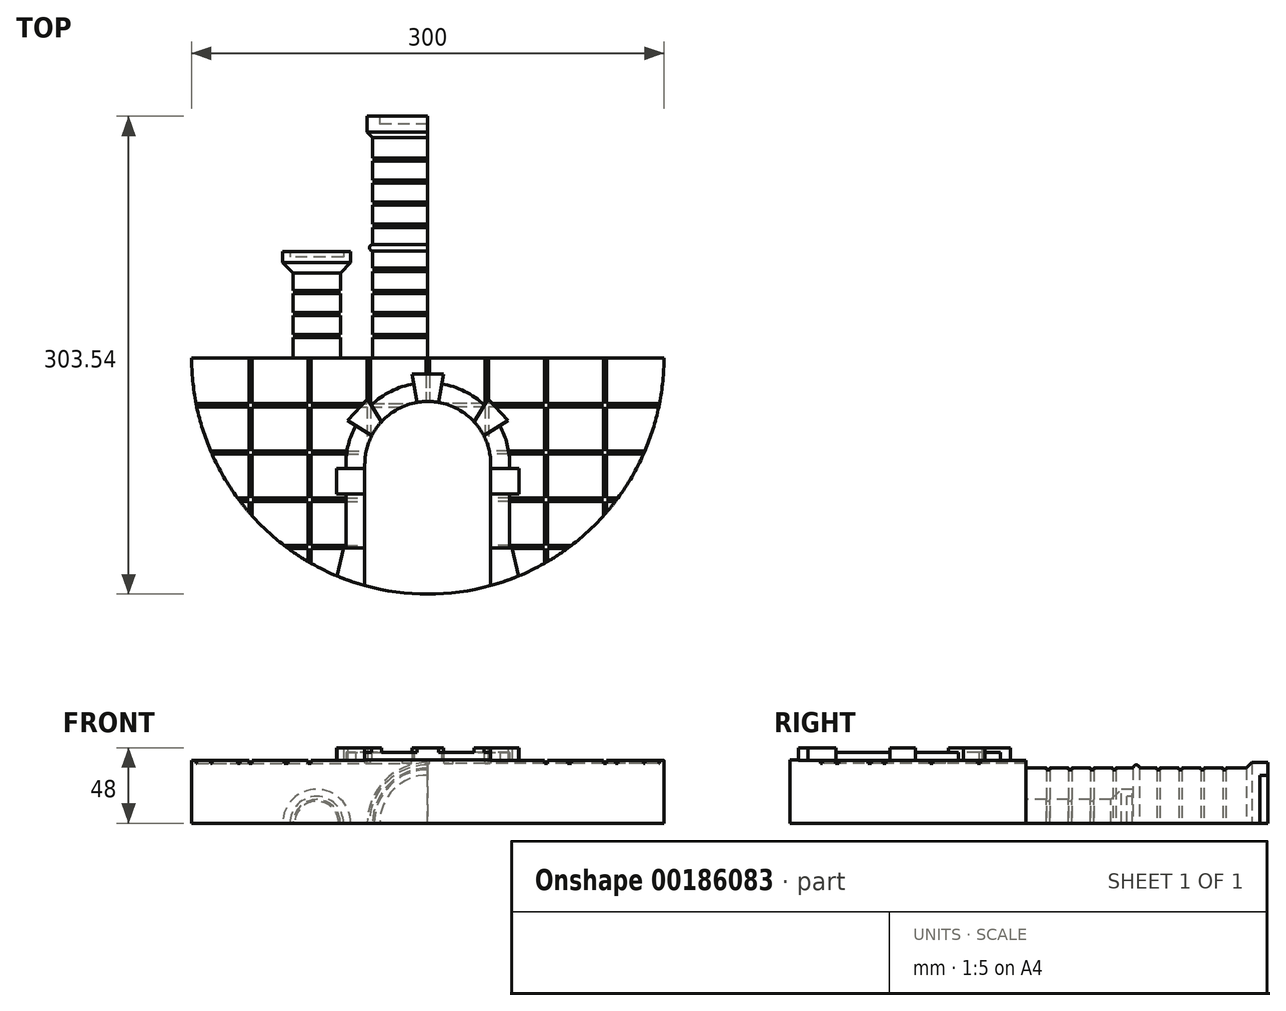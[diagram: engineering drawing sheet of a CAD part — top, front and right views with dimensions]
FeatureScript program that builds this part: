
annotation { "Feature Type Name" : "Feature", "Feature Type Description" : "" }
export const myFeature = defineFeature(function(context is Context, id is Id, definition is map)
    precondition{}
    {
        {
            var Q0;
            Q0=qCreatedBy(makeId("Top.planeOp"),FACE);
            var sketch = newSketch(context, id + "F0", { "sketchPlane" : qUnion([Q0])});
            skLineSegment(sketch, "E0", {"start": v(0, 136.15) * mm, "end": v(0, -317.95) * mm, "construction": true});
            skLineSegment(sketch, "E1.0", {"start": v(-150, 44.84) * mm, "end": v(-150, -145.55) * mm});
            skLineSegment(sketch, "E2", {"start": v(-150, 44.84) * mm, "end": v(0, 44.84) * mm});
            skArc(sketch, "E3", {"start": v(-150, -145.55) * mm, "mid": v(-106.07, -251.62) * mm, "end": v(0, -295.55) * mm});
            skLineSegment(sketch, "E4", {"start": v(-157.24, -145.55) * mm, "end": v(0, -145.55) * mm});
            skLineSegment(sketch, "E5", {"start": v(0, -145.55) * mm, "end": v(0, -295.55) * mm});
            skSolve(sketch);
        }
        {
            var Q0;
            Q0 = qSketchRegion(id + "F0", true);
            extrude(context, id + "F1", {"entities" : qUnion([Q0]), "depth" : 40 * mm});
        }
        {
            var Q0;
            Q0=makeQuery(id+"F1.opExtrude","CAP_FACE",FACE,{"disambiguationData":[OSD([sQuery(id+"F0.wireOp",EDGE,"E3"),sQuery(id+"F0.wireOp",EDGE,"E4"),sQuery(id+"F0.wireOp",EDGE,"E5")])],"isStart":false});
            var sketch = newSketch(context, id + "F2", { "sketchPlane" : qUnion([Q0])});
            skLineSegment(sketch, "E6.0", {"start": v(-150, -174.55) * mm, "end": v(0, -174.55) * mm});
            skLineSegment(sketch, "E7.0", {"start": v(-150, -176.55) * mm, "end": v(0, -176.55) * mm});
            skLineSegment(sketch, "E8.0", {"start": v(-150, -204.55) * mm, "end": v(0, -204.55) * mm});
            skLineSegment(sketch, "E9.0", {"start": v(-150, -206.55) * mm, "end": v(0, -206.55) * mm});
            skLineSegment(sketch, "E10.0", {"start": v(-150, -234.55) * mm, "end": v(0, -234.55) * mm});
            skLineSegment(sketch, "E11.0", {"start": v(-150, -236.55) * mm, "end": v(0, -236.55) * mm});
            skLineSegment(sketch, "E12.0", {"start": v(-150, -264.55) * mm, "end": v(0, -264.55) * mm});
            skLineSegment(sketch, "E13.0", {"start": v(-150, -266.55) * mm, "end": v(0, -266.55) * mm});
            skLineSegment(sketch, "E14.0", {"start": v(-1, -140.7) * mm, "end": v(-1, -302.51) * mm});
            skLineSegment(sketch, "E15.0", {"start": v(-38.5, -140.42) * mm, "end": v(-38.5, -295.55) * mm});
            skLineSegment(sketch, "E16.0", {"start": v(-36.5, -139.03) * mm, "end": v(-36.5, -295.55) * mm});
            skLineSegment(sketch, "E17.0", {"start": v(-76, -139.3) * mm, "end": v(-76, -295.55) * mm});
            skLineSegment(sketch, "E18.0", {"start": v(-74, -139.03) * mm, "end": v(-74, -295.55) * mm});
            skLineSegment(sketch, "E19.0", {"start": v(-111.5, -140.42) * mm, "end": v(-111.5, -295.55) * mm});
            skLineSegment(sketch, "E20.0", {"start": v(-113.5, -139.3) * mm, "end": v(-113.5, -295.55) * mm});
            skLineSegment(sketch, "E21", {"start": v(-1, -140.7) * mm, "end": v(2.08, -140.7) * mm});
            skLineSegment(sketch, "E22", {"start": v(2.08, -140.7) * mm, "end": v(2.08, -302.51) * mm});
            skLineSegment(sketch, "E23", {"start": v(2.08, -302.51) * mm, "end": v(-1, -302.51) * mm});
            skLineSegment(sketch, "E24", {"start": v(-113.5, -139.3) * mm, "end": v(-111.5, -140.42) * mm});
            skLineSegment(sketch, "E25", {"start": v(-76, -139.3) * mm, "end": v(-74, -139.03) * mm});
            skLineSegment(sketch, "E26", {"start": v(-38.5, -140.42) * mm, "end": v(-36.5, -139.03) * mm});
            skLineSegment(sketch, "E27", {"start": v(-38.5, -295.55) * mm, "end": v(-36.5, -295.55) * mm});
            skLineSegment(sketch, "E28", {"start": v(-74, -295.55) * mm, "end": v(-76, -295.55) * mm});
            skLineSegment(sketch, "E29", {"start": v(-111.5, -295.55) * mm, "end": v(-113.5, -295.55) * mm});
            skLineSegment(sketch, "E30", {"start": v(-150, -264.55) * mm, "end": v(-150, -266.55) * mm});
            skLineSegment(sketch, "E31", {"start": v(-150, -234.55) * mm, "end": v(-150, -236.55) * mm});
            skLineSegment(sketch, "E32", {"start": v(-150, -204.55) * mm, "end": v(-150, -206.55) * mm});
            skLineSegment(sketch, "E33", {"start": v(-150, -174.55) * mm, "end": v(-150, -176.55) * mm});
            skSolve(sketch);
        }
        {
            var Q0;
            {var subQ0=sQuery(id+"F2.wireOp",EDGE,"E30");Q0=makeQuery(id+"F2.imprint","IMPRINT",FACE,{"disambiguationData":[TD([[makeQuery(id+"F2.imprint","IMPRINT",EDGE,{"derivedFrom":subQ0}),1.0]])]});}
            var Q1;
            {var subQ5=sQuery(id+"F2.wireOp",EDGE,"E29");Q1=makeQuery(id+"F2.imprint","IMPRINT",FACE,{"disambiguationData":[TD([[makeQuery(id+"F2.imprint","IMPRINT",EDGE,{"derivedFrom":subQ5}),-1.0]])]});}
            var Q2;
            {var subQ0=sQuery(id+"F2.wireOp",EDGE,"E20.0");var subQ1=sQuery(id+"F2.wireOp",EDGE,"E6.0");var subQ2=makeQuery(id+"F2.imprint","INTERSECT",VERTEX,{"derivedFrom":[subQ1,subQ0]});Q2=makeQuery(id+"F2.imprint","IMPRINT",FACE,{"disambiguationData":[TD([[makeQuery(id+"F2.imprint","IMPRINT",EDGE,{"disambiguationData":[TD([[subQ2,-1.0]])],"derivedFrom":subQ1}),-1.0]])]});}
            var Q3;
            {var subQ0=sQuery(id+"F2.wireOp",EDGE,"E19.0");var subQ1=sQuery(id+"F2.wireOp",EDGE,"E6.0");var subQ2=makeQuery(id+"F2.imprint","INTERSECT",VERTEX,{"derivedFrom":[subQ1,subQ0]});Q3=makeQuery(id+"F2.imprint","IMPRINT",FACE,{"disambiguationData":[TD([[makeQuery(id+"F2.imprint","IMPRINT",EDGE,{"disambiguationData":[TD([[subQ2,-1.0]])],"derivedFrom":subQ1}),-1.0]])]});}
            var Q4;
            {var subQ0=sQuery(id+"F2.wireOp",EDGE,"E17.0");var subQ1=sQuery(id+"F2.wireOp",EDGE,"E6.0");var subQ2=makeQuery(id+"F2.imprint","INTERSECT",VERTEX,{"derivedFrom":[subQ1,subQ0]});Q4=makeQuery(id+"F2.imprint","IMPRINT",FACE,{"disambiguationData":[TD([[makeQuery(id+"F2.imprint","IMPRINT",EDGE,{"disambiguationData":[TD([[subQ2,-1.0]])],"derivedFrom":subQ1}),-1.0]])]});}
            var Q5;
            {var subQ0=sQuery(id+"F2.wireOp",EDGE,"E18.0");var subQ1=sQuery(id+"F2.wireOp",EDGE,"E6.0");var subQ2=makeQuery(id+"F2.imprint","INTERSECT",VERTEX,{"derivedFrom":[subQ1,subQ0]});Q5=makeQuery(id+"F2.imprint","IMPRINT",FACE,{"disambiguationData":[TD([[makeQuery(id+"F2.imprint","IMPRINT",EDGE,{"disambiguationData":[TD([[subQ2,-1.0]])],"derivedFrom":subQ1}),-1.0]])]});}
            var Q6;
            {var subQ0=sQuery(id+"F2.wireOp",EDGE,"E15.0");var subQ1=sQuery(id+"F2.wireOp",EDGE,"E6.0");var subQ2=makeQuery(id+"F2.imprint","INTERSECT",VERTEX,{"derivedFrom":[subQ1,subQ0]});Q6=makeQuery(id+"F2.imprint","IMPRINT",FACE,{"disambiguationData":[TD([[makeQuery(id+"F2.imprint","IMPRINT",EDGE,{"disambiguationData":[TD([[subQ2,-1.0]])],"derivedFrom":subQ1}),-1.0]])]});}
            var Q7;
            {var subQ0=sQuery(id+"F2.wireOp",EDGE,"E16.0");var subQ1=sQuery(id+"F2.wireOp",EDGE,"E6.0");var subQ2=makeQuery(id+"F2.imprint","INTERSECT",VERTEX,{"derivedFrom":[subQ1,subQ0]});Q7=makeQuery(id+"F2.imprint","IMPRINT",FACE,{"disambiguationData":[TD([[makeQuery(id+"F2.imprint","IMPRINT",EDGE,{"disambiguationData":[TD([[subQ2,-1.0]])],"derivedFrom":subQ1}),-1.0]])]});}
            var Q8;
            {var subQ0=sQuery(id+"F2.wireOp",EDGE,"E20.0");var subQ1=sQuery(id+"F2.wireOp",EDGE,"E7.0");var subQ2=makeQuery(id+"F2.imprint","INTERSECT",VERTEX,{"derivedFrom":[subQ1,subQ0]});Q8=makeQuery(id+"F2.imprint","IMPRINT",FACE,{"disambiguationData":[TD([[makeQuery(id+"F2.imprint","IMPRINT",EDGE,{"disambiguationData":[TD([[subQ2,-1.0]])],"derivedFrom":subQ1}),-1.0]])]});}
            var Q9;
            {var subQ0=sQuery(id+"F2.wireOp",EDGE,"E20.0");var subQ1=sQuery(id+"F2.wireOp",EDGE,"E8.0");var subQ2=makeQuery(id+"F2.imprint","INTERSECT",VERTEX,{"derivedFrom":[subQ1,subQ0]});Q9=makeQuery(id+"F2.imprint","IMPRINT",FACE,{"disambiguationData":[TD([[makeQuery(id+"F2.imprint","IMPRINT",EDGE,{"disambiguationData":[TD([[subQ2,-1.0]])],"derivedFrom":subQ1}),-1.0]])]});}
            var Q10;
            {var subQ0=sQuery(id+"F2.wireOp",EDGE,"E20.0");var subQ1=sQuery(id+"F2.wireOp",EDGE,"E9.0");var subQ2=makeQuery(id+"F2.imprint","INTERSECT",VERTEX,{"derivedFrom":[subQ1,subQ0]});Q10=makeQuery(id+"F2.imprint","IMPRINT",FACE,{"disambiguationData":[TD([[makeQuery(id+"F2.imprint","IMPRINT",EDGE,{"disambiguationData":[TD([[subQ2,-1.0]])],"derivedFrom":subQ1}),-1.0]])]});}
            var Q11;
            {var subQ0=sQuery(id+"F2.wireOp",EDGE,"E20.0");var subQ1=sQuery(id+"F2.wireOp",EDGE,"E12.0");var subQ2=makeQuery(id+"F2.imprint","INTERSECT",VERTEX,{"derivedFrom":[subQ1,subQ0]});Q11=makeQuery(id+"F2.imprint","IMPRINT",FACE,{"disambiguationData":[TD([[makeQuery(id+"F2.imprint","IMPRINT",EDGE,{"disambiguationData":[TD([[subQ2,-1.0]])],"derivedFrom":subQ1}),-1.0]])]});}
            var Q12;
            {var subQ0=sQuery(id+"F2.wireOp",EDGE,"E17.0");var subQ1=sQuery(id+"F2.wireOp",EDGE,"E12.0");var subQ2=makeQuery(id+"F2.imprint","INTERSECT",VERTEX,{"derivedFrom":[subQ1,subQ0]});Q12=makeQuery(id+"F2.imprint","IMPRINT",FACE,{"disambiguationData":[TD([[makeQuery(id+"F2.imprint","IMPRINT",EDGE,{"disambiguationData":[TD([[subQ2,-1.0]])],"derivedFrom":subQ1}),-1.0]])]});}
            var Q13;
            {var subQ0=sQuery(id+"F2.wireOp",EDGE,"E18.0");var subQ1=sQuery(id+"F2.wireOp",EDGE,"E12.0");var subQ2=makeQuery(id+"F2.imprint","INTERSECT",VERTEX,{"derivedFrom":[subQ1,subQ0]});Q13=makeQuery(id+"F2.imprint","IMPRINT",FACE,{"disambiguationData":[TD([[makeQuery(id+"F2.imprint","IMPRINT",EDGE,{"disambiguationData":[TD([[subQ2,-1.0]])],"derivedFrom":subQ1}),-1.0]])]});}
            var Q14;
            {var subQ0=sQuery(id+"F2.wireOp",EDGE,"E15.0");var subQ1=sQuery(id+"F2.wireOp",EDGE,"E12.0");var subQ2=makeQuery(id+"F2.imprint","INTERSECT",VERTEX,{"derivedFrom":[subQ1,subQ0]});Q14=makeQuery(id+"F2.imprint","IMPRINT",FACE,{"disambiguationData":[TD([[makeQuery(id+"F2.imprint","IMPRINT",EDGE,{"disambiguationData":[TD([[subQ2,-1.0]])],"derivedFrom":subQ1}),-1.0]])]});}
            var Q15;
            {var subQ0=sQuery(id+"F2.wireOp",EDGE,"E16.0");var subQ1=sQuery(id+"F2.wireOp",EDGE,"E12.0");var subQ2=makeQuery(id+"F2.imprint","INTERSECT",VERTEX,{"derivedFrom":[subQ1,subQ0]});Q15=makeQuery(id+"F2.imprint","IMPRINT",FACE,{"disambiguationData":[TD([[makeQuery(id+"F2.imprint","IMPRINT",EDGE,{"disambiguationData":[TD([[subQ2,-1.0]])],"derivedFrom":subQ1}),-1.0]])]});}
            var Q16;
            {var subQ0=sQuery(id+"F2.wireOp",EDGE,"E33");Q16=makeQuery(id+"F2.imprint","IMPRINT",FACE,{"disambiguationData":[TD([[makeQuery(id+"F2.imprint","IMPRINT",EDGE,{"derivedFrom":subQ0}),1.0]])]});}
            var Q17;
            {var subQ0=sQuery(id+"F2.wireOp",EDGE,"E32");Q17=makeQuery(id+"F2.imprint","IMPRINT",FACE,{"disambiguationData":[TD([[makeQuery(id+"F2.imprint","IMPRINT",EDGE,{"derivedFrom":subQ0}),1.0]])]});}
            var Q18;
            {var subQ0=sQuery(id+"F2.wireOp",EDGE,"E31");Q18=makeQuery(id+"F2.imprint","IMPRINT",FACE,{"disambiguationData":[TD([[makeQuery(id+"F2.imprint","IMPRINT",EDGE,{"derivedFrom":subQ0}),1.0]])]});}
            var Q19;
            {var subQ0=sQuery(id+"F2.wireOp",EDGE,"E26");Q19=makeQuery(id+"F2.imprint","IMPRINT",FACE,{"disambiguationData":[TD([[makeQuery(id+"F2.imprint","IMPRINT",EDGE,{"derivedFrom":subQ0}),-1.0]])]});}
            var Q20;
            {var subQ0=sQuery(id+"F2.wireOp",EDGE,"E27");Q20=makeQuery(id+"F2.imprint","IMPRINT",FACE,{"disambiguationData":[TD([[makeQuery(id+"F2.imprint","IMPRINT",EDGE,{"derivedFrom":subQ0}),1.0]])]});}
            var Q21;
            {var subQ0=sQuery(id+"F2.wireOp",EDGE,"E25");Q21=makeQuery(id+"F2.imprint","IMPRINT",FACE,{"disambiguationData":[TD([[makeQuery(id+"F2.imprint","IMPRINT",EDGE,{"derivedFrom":subQ0}),-1.0]])]});}
            var Q22;
            {var subQ0=sQuery(id+"F2.wireOp",EDGE,"E28");Q22=makeQuery(id+"F2.imprint","IMPRINT",FACE,{"disambiguationData":[TD([[makeQuery(id+"F2.imprint","IMPRINT",EDGE,{"derivedFrom":subQ0}),-1.0]])]});}
            var Q23;
            {var subQ0=sQuery(id+"F2.wireOp",EDGE,"E24");Q23=makeQuery(id+"F2.imprint","IMPRINT",FACE,{"disambiguationData":[TD([[makeQuery(id+"F2.imprint","IMPRINT",EDGE,{"derivedFrom":subQ0}),-1.0]])]});}
            var Q24;
            {var subQ0=sQuery(id+"F2.wireOp",EDGE,"E20.0");var subQ1=sQuery(id+"F2.wireOp",EDGE,"E12.0");var subQ2=makeQuery(id+"F2.imprint","INTERSECT",VERTEX,{"derivedFrom":[subQ1,subQ0]});Q24=makeQuery(id+"F2.imprint","IMPRINT",FACE,{"disambiguationData":[TD([[makeQuery(id+"F2.imprint","IMPRINT",EDGE,{"disambiguationData":[TD([[subQ2,-1.0]])],"derivedFrom":subQ1}),1.0]])]});}
            var Q25;
            {var subQ0=sQuery(id+"F2.wireOp",EDGE,"E19.0");var subQ1=sQuery(id+"F2.wireOp",EDGE,"E12.0");var subQ2=makeQuery(id+"F2.imprint","INTERSECT",VERTEX,{"derivedFrom":[subQ1,subQ0]});Q25=makeQuery(id+"F2.imprint","IMPRINT",FACE,{"disambiguationData":[TD([[makeQuery(id+"F2.imprint","IMPRINT",EDGE,{"disambiguationData":[TD([[subQ2,-1.0]])],"derivedFrom":subQ1}),-1.0]])]});}
            var Q26;
            {var subQ0=sQuery(id+"F2.wireOp",EDGE,"E20.0");var subQ1=sQuery(id+"F2.wireOp",EDGE,"E6.0");var subQ2=makeQuery(id+"F2.imprint","INTERSECT",VERTEX,{"derivedFrom":[subQ1,subQ0]});Q26=makeQuery(id+"F2.imprint","IMPRINT",FACE,{"disambiguationData":[TD([[makeQuery(id+"F2.imprint","IMPRINT",EDGE,{"disambiguationData":[TD([[subQ2,1.0]])],"derivedFrom":subQ1}),-1.0]])]});}
            var Q27;
            {var subQ0=sQuery(id+"F2.wireOp",EDGE,"E20.0");var subQ1=sQuery(id+"F2.wireOp",EDGE,"E6.0");var subQ2=makeQuery(id+"F2.imprint","INTERSECT",VERTEX,{"derivedFrom":[subQ1,subQ0]});Q27=makeQuery(id+"F2.imprint","IMPRINT",FACE,{"disambiguationData":[TD([[makeQuery(id+"F2.imprint","IMPRINT",EDGE,{"disambiguationData":[TD([[subQ2,-1.0]])],"derivedFrom":subQ1}),1.0]])]});}
            var Q28;
            {var subQ0=sQuery(id+"F2.wireOp",EDGE,"E17.0");var subQ1=sQuery(id+"F2.wireOp",EDGE,"E6.0");var subQ2=makeQuery(id+"F2.imprint","INTERSECT",VERTEX,{"derivedFrom":[subQ1,subQ0]});Q28=makeQuery(id+"F2.imprint","IMPRINT",FACE,{"disambiguationData":[TD([[makeQuery(id+"F2.imprint","IMPRINT",EDGE,{"disambiguationData":[TD([[subQ2,-1.0]])],"derivedFrom":subQ1}),1.0]])]});}
            var Q29;
            {var subQ0=sQuery(id+"F2.wireOp",EDGE,"E15.0");var subQ1=sQuery(id+"F2.wireOp",EDGE,"E6.0");var subQ2=makeQuery(id+"F2.imprint","INTERSECT",VERTEX,{"derivedFrom":[subQ1,subQ0]});Q29=makeQuery(id+"F2.imprint","IMPRINT",FACE,{"disambiguationData":[TD([[makeQuery(id+"F2.imprint","IMPRINT",EDGE,{"disambiguationData":[TD([[subQ2,-1.0]])],"derivedFrom":subQ1}),1.0]])]});}
            var Q30;
            {var subQ0=sQuery(id+"F2.wireOp",EDGE,"E6.0");var subQ1=makeQuery(id+"F1.opExtrude","CAP_EDGE",EDGE,{"disambiguationData":[OSD([sQuery(id+"F0.wireOp",EDGE,"E5")])],"isStart":false});var subQ2=makeQuery(id+"F2.imprint","INTERSECT",VERTEX,{"derivedFrom":[subQ1,subQ0]});Q30=makeQuery(id+"F2.imprint","IMPRINT",FACE,{"disambiguationData":[TD([[makeQuery(id+"F2.imprint","IMPRINT",EDGE,{"disambiguationData":[TD([[subQ2,1.0]])],"derivedFrom":subQ0}),-1.0]])]});}
            var Q31;
            {var subQ0=sQuery(id+"F2.wireOp",EDGE,"E7.0");var subQ1=makeQuery(id+"F1.opExtrude","CAP_EDGE",EDGE,{"disambiguationData":[OSD([sQuery(id+"F0.wireOp",EDGE,"E5")])],"isStart":false});var subQ2=makeQuery(id+"F2.imprint","INTERSECT",VERTEX,{"derivedFrom":[subQ1,subQ0]});Q31=makeQuery(id+"F2.imprint","IMPRINT",FACE,{"disambiguationData":[TD([[makeQuery(id+"F2.imprint","IMPRINT",EDGE,{"disambiguationData":[TD([[subQ2,1.0]])],"derivedFrom":subQ0}),-1.0]])]});}
            var Q32;
            {var subQ0=sQuery(id+"F2.wireOp",EDGE,"E20.0");var subQ1=sQuery(id+"F2.wireOp",EDGE,"E8.0");var subQ2=makeQuery(id+"F2.imprint","INTERSECT",VERTEX,{"derivedFrom":[subQ1,subQ0]});Q32=makeQuery(id+"F2.imprint","IMPRINT",FACE,{"disambiguationData":[TD([[makeQuery(id+"F2.imprint","IMPRINT",EDGE,{"disambiguationData":[TD([[subQ2,1.0]])],"derivedFrom":subQ1}),-1.0]])]});}
            var Q33;
            {var subQ0=sQuery(id+"F2.wireOp",EDGE,"E8.0");var subQ1=makeQuery(id+"F1.opExtrude","CAP_EDGE",EDGE,{"disambiguationData":[OSD([sQuery(id+"F0.wireOp",EDGE,"E5")])],"isStart":false});var subQ2=makeQuery(id+"F2.imprint","INTERSECT",VERTEX,{"derivedFrom":[subQ1,subQ0]});Q33=makeQuery(id+"F2.imprint","IMPRINT",FACE,{"disambiguationData":[TD([[makeQuery(id+"F2.imprint","IMPRINT",EDGE,{"disambiguationData":[TD([[subQ2,1.0]])],"derivedFrom":subQ0}),-1.0]])]});}
            var Q34;
            {var subQ0=sQuery(id+"F2.wireOp",EDGE,"E9.0");var subQ1=makeQuery(id+"F1.opExtrude","CAP_EDGE",EDGE,{"disambiguationData":[OSD([sQuery(id+"F0.wireOp",EDGE,"E5")])],"isStart":false});var subQ2=makeQuery(id+"F2.imprint","INTERSECT",VERTEX,{"derivedFrom":[subQ1,subQ0]});Q34=makeQuery(id+"F2.imprint","IMPRINT",FACE,{"disambiguationData":[TD([[makeQuery(id+"F2.imprint","IMPRINT",EDGE,{"disambiguationData":[TD([[subQ2,1.0]])],"derivedFrom":subQ0}),-1.0]])]});}
            var Q35;
            {var subQ0=sQuery(id+"F2.wireOp",EDGE,"E20.0");var subQ1=sQuery(id+"F2.wireOp",EDGE,"E10.0");var subQ2=makeQuery(id+"F2.imprint","INTERSECT",VERTEX,{"derivedFrom":[subQ1,subQ0]});Q35=makeQuery(id+"F2.imprint","IMPRINT",FACE,{"disambiguationData":[TD([[makeQuery(id+"F2.imprint","IMPRINT",EDGE,{"disambiguationData":[TD([[subQ2,1.0]])],"derivedFrom":subQ1}),-1.0]])]});}
            var Q36;
            {var subQ0=sQuery(id+"F2.wireOp",EDGE,"E10.0");var subQ1=makeQuery(id+"F1.opExtrude","CAP_EDGE",EDGE,{"disambiguationData":[OSD([sQuery(id+"F0.wireOp",EDGE,"E5")])],"isStart":false});var subQ2=makeQuery(id+"F2.imprint","INTERSECT",VERTEX,{"derivedFrom":[subQ1,subQ0]});Q36=makeQuery(id+"F2.imprint","IMPRINT",FACE,{"disambiguationData":[TD([[makeQuery(id+"F2.imprint","IMPRINT",EDGE,{"disambiguationData":[TD([[subQ2,1.0]])],"derivedFrom":subQ0}),-1.0]])]});}
            var Q37;
            {var subQ0=sQuery(id+"F2.wireOp",EDGE,"E20.0");var subQ1=sQuery(id+"F2.wireOp",EDGE,"E11.0");var subQ2=makeQuery(id+"F2.imprint","INTERSECT",VERTEX,{"derivedFrom":[subQ1,subQ0]});Q37=makeQuery(id+"F2.imprint","IMPRINT",FACE,{"disambiguationData":[TD([[makeQuery(id+"F2.imprint","IMPRINT",EDGE,{"disambiguationData":[TD([[subQ2,-1.0]])],"derivedFrom":subQ1}),-1.0]])]});}
            var Q38;
            {var subQ0=sQuery(id+"F2.wireOp",EDGE,"E11.0");var subQ1=makeQuery(id+"F1.opExtrude","CAP_EDGE",EDGE,{"disambiguationData":[OSD([sQuery(id+"F0.wireOp",EDGE,"E5")])],"isStart":false});var subQ2=makeQuery(id+"F2.imprint","INTERSECT",VERTEX,{"derivedFrom":[subQ1,subQ0]});Q38=makeQuery(id+"F2.imprint","IMPRINT",FACE,{"disambiguationData":[TD([[makeQuery(id+"F2.imprint","IMPRINT",EDGE,{"disambiguationData":[TD([[subQ2,1.0]])],"derivedFrom":subQ0}),-1.0]])]});}
            var Q39;
            {var subQ0=sQuery(id+"F2.wireOp",EDGE,"E17.0");var subQ1=sQuery(id+"F2.wireOp",EDGE,"E12.0");var subQ2=makeQuery(id+"F2.imprint","INTERSECT",VERTEX,{"derivedFrom":[subQ1,subQ0]});Q39=makeQuery(id+"F2.imprint","IMPRINT",FACE,{"disambiguationData":[TD([[makeQuery(id+"F2.imprint","IMPRINT",EDGE,{"disambiguationData":[TD([[subQ2,1.0]])],"derivedFrom":subQ1}),-1.0]])]});}
            var Q40;
            {var subQ0=sQuery(id+"F2.wireOp",EDGE,"E12.0");var subQ1=makeQuery(id+"F1.opExtrude","CAP_EDGE",EDGE,{"disambiguationData":[OSD([sQuery(id+"F0.wireOp",EDGE,"E5")])],"isStart":false});var subQ2=makeQuery(id+"F2.imprint","INTERSECT",VERTEX,{"derivedFrom":[subQ1,subQ0]});Q40=makeQuery(id+"F2.imprint","IMPRINT",FACE,{"disambiguationData":[TD([[makeQuery(id+"F2.imprint","IMPRINT",EDGE,{"disambiguationData":[TD([[subQ2,1.0]])],"derivedFrom":subQ0}),-1.0]])]});}
            var Q41;
            {var subQ0=sQuery(id+"F2.wireOp",EDGE,"E17.0");var subQ1=sQuery(id+"F2.wireOp",EDGE,"E13.0");var subQ2=makeQuery(id+"F2.imprint","INTERSECT",VERTEX,{"derivedFrom":[subQ1,subQ0]});Q41=makeQuery(id+"F2.imprint","IMPRINT",FACE,{"disambiguationData":[TD([[makeQuery(id+"F2.imprint","IMPRINT",EDGE,{"disambiguationData":[TD([[subQ2,-1.0]])],"derivedFrom":subQ1}),-1.0]])]});}
            var Q42;
            {var subQ0=sQuery(id+"F2.wireOp",EDGE,"E15.0");var subQ1=sQuery(id+"F2.wireOp",EDGE,"E13.0");var subQ2=makeQuery(id+"F2.imprint","INTERSECT",VERTEX,{"derivedFrom":[subQ1,subQ0]});Q42=makeQuery(id+"F2.imprint","IMPRINT",FACE,{"disambiguationData":[TD([[makeQuery(id+"F2.imprint","IMPRINT",EDGE,{"disambiguationData":[TD([[subQ2,-1.0]])],"derivedFrom":subQ1}),-1.0]])]});}
            var Q43;
            {var subQ0=sQuery(id+"F2.wireOp",EDGE,"E6.0");var subQ1=makeQuery(id+"F1.opExtrude","CAP_EDGE",EDGE,{"disambiguationData":[OSD([sQuery(id+"F0.wireOp",EDGE,"E5")])],"isStart":false});var subQ2=makeQuery(id+"F2.imprint","INTERSECT",VERTEX,{"derivedFrom":[subQ1,subQ0]});Q43=makeQuery(id+"F2.imprint","IMPRINT",FACE,{"disambiguationData":[TD([[makeQuery(id+"F2.imprint","IMPRINT",EDGE,{"disambiguationData":[TD([[subQ2,1.0]])],"derivedFrom":subQ0}),1.0]])]});}
            var Q44;
            {var subQ0=sQuery(id+"F2.wireOp",EDGE,"E13.0");var subQ1=makeQuery(id+"F1.opExtrude","CAP_EDGE",EDGE,{"disambiguationData":[OSD([sQuery(id+"F0.wireOp",EDGE,"E5")])],"isStart":false});var subQ2=makeQuery(id+"F2.imprint","INTERSECT",VERTEX,{"derivedFrom":[subQ1,subQ0]});Q44=makeQuery(id+"F2.imprint","IMPRINT",FACE,{"disambiguationData":[TD([[makeQuery(id+"F2.imprint","IMPRINT",EDGE,{"disambiguationData":[TD([[subQ2,1.0]])],"derivedFrom":subQ0}),-1.0]])]});}
            var Q45;
            {var subQ12=sQuery(id+"F2.wireOp",EDGE,"E21");Q45=makeQuery(id+"F2.imprint","IMPRINT",FACE,{"disambiguationData":[TD([[makeQuery(id+"F2.imprint","IMPRINT",EDGE,{"derivedFrom":subQ12}),-1.0]])]});}
            var Q46;
            {var subQ0=sQuery(id+"F2.wireOp",EDGE,"E17.0");var subQ1=sQuery(id+"F2.wireOp",EDGE,"E7.0");var subQ2=makeQuery(id+"F2.imprint","INTERSECT",VERTEX,{"derivedFrom":[subQ1,subQ0]});Q46=makeQuery(id+"F2.imprint","IMPRINT",FACE,{"disambiguationData":[TD([[makeQuery(id+"F2.imprint","IMPRINT",EDGE,{"disambiguationData":[TD([[subQ2,-1.0]])],"derivedFrom":subQ1}),-1.0]])]});}
            var Q47;
            {var subQ0=sQuery(id+"F2.wireOp",EDGE,"E19.0");var subQ1=sQuery(id+"F2.wireOp",EDGE,"E8.0");var subQ2=makeQuery(id+"F2.imprint","INTERSECT",VERTEX,{"derivedFrom":[subQ1,subQ0]});Q47=makeQuery(id+"F2.imprint","IMPRINT",FACE,{"disambiguationData":[TD([[makeQuery(id+"F2.imprint","IMPRINT",EDGE,{"disambiguationData":[TD([[subQ2,-1.0]])],"derivedFrom":subQ1}),-1.0]])]});}
            var Q48;
            {var subQ0=sQuery(id+"F2.wireOp",EDGE,"E18.0");var subQ1=sQuery(id+"F2.wireOp",EDGE,"E8.0");var subQ2=makeQuery(id+"F2.imprint","INTERSECT",VERTEX,{"derivedFrom":[subQ1,subQ0]});Q48=makeQuery(id+"F2.imprint","IMPRINT",FACE,{"disambiguationData":[TD([[makeQuery(id+"F2.imprint","IMPRINT",EDGE,{"disambiguationData":[TD([[subQ2,-1.0]])],"derivedFrom":subQ1}),-1.0]])]});}
            var Q49;
            {var subQ0=sQuery(id+"F2.wireOp",EDGE,"E15.0");var subQ1=sQuery(id+"F2.wireOp",EDGE,"E7.0");var subQ2=makeQuery(id+"F2.imprint","INTERSECT",VERTEX,{"derivedFrom":[subQ1,subQ0]});Q49=makeQuery(id+"F2.imprint","IMPRINT",FACE,{"disambiguationData":[TD([[makeQuery(id+"F2.imprint","IMPRINT",EDGE,{"disambiguationData":[TD([[subQ2,-1.0]])],"derivedFrom":subQ1}),-1.0]])]});}
            var Q50;
            {var subQ0=sQuery(id+"F2.wireOp",EDGE,"E16.0");var subQ1=sQuery(id+"F2.wireOp",EDGE,"E8.0");var subQ2=makeQuery(id+"F2.imprint","INTERSECT",VERTEX,{"derivedFrom":[subQ1,subQ0]});Q50=makeQuery(id+"F2.imprint","IMPRINT",FACE,{"disambiguationData":[TD([[makeQuery(id+"F2.imprint","IMPRINT",EDGE,{"disambiguationData":[TD([[subQ2,-1.0]])],"derivedFrom":subQ1}),-1.0]])]});}
            var Q51;
            {var subQ0=sQuery(id+"F2.wireOp",EDGE,"E16.0");var subQ1=sQuery(id+"F2.wireOp",EDGE,"E10.0");var subQ2=makeQuery(id+"F2.imprint","INTERSECT",VERTEX,{"derivedFrom":[subQ1,subQ0]});Q51=makeQuery(id+"F2.imprint","IMPRINT",FACE,{"disambiguationData":[TD([[makeQuery(id+"F2.imprint","IMPRINT",EDGE,{"disambiguationData":[TD([[subQ2,-1.0]])],"derivedFrom":subQ1}),-1.0]])]});}
            var Q52;
            {var subQ0=sQuery(id+"F2.wireOp",EDGE,"E18.0");var subQ1=sQuery(id+"F2.wireOp",EDGE,"E10.0");var subQ2=makeQuery(id+"F2.imprint","INTERSECT",VERTEX,{"derivedFrom":[subQ1,subQ0]});Q52=makeQuery(id+"F2.imprint","IMPRINT",FACE,{"disambiguationData":[TD([[makeQuery(id+"F2.imprint","IMPRINT",EDGE,{"disambiguationData":[TD([[subQ2,-1.0]])],"derivedFrom":subQ1}),-1.0]])]});}
            var Q53;
            {var subQ0=sQuery(id+"F2.wireOp",EDGE,"E15.0");var subQ1=sQuery(id+"F2.wireOp",EDGE,"E9.0");var subQ2=makeQuery(id+"F2.imprint","INTERSECT",VERTEX,{"derivedFrom":[subQ1,subQ0]});Q53=makeQuery(id+"F2.imprint","IMPRINT",FACE,{"disambiguationData":[TD([[makeQuery(id+"F2.imprint","IMPRINT",EDGE,{"disambiguationData":[TD([[subQ2,-1.0]])],"derivedFrom":subQ1}),-1.0]])]});}
            var Q54;
            {var subQ0=sQuery(id+"F2.wireOp",EDGE,"E15.0");var subQ1=sQuery(id+"F2.wireOp",EDGE,"E11.0");var subQ2=makeQuery(id+"F2.imprint","INTERSECT",VERTEX,{"derivedFrom":[subQ1,subQ0]});Q54=makeQuery(id+"F2.imprint","IMPRINT",FACE,{"disambiguationData":[TD([[makeQuery(id+"F2.imprint","IMPRINT",EDGE,{"disambiguationData":[TD([[subQ2,-1.0]])],"derivedFrom":subQ1}),-1.0]])]});}
            var Q55;
            {var subQ0=sQuery(id+"F2.wireOp",EDGE,"E17.0");var subQ1=sQuery(id+"F2.wireOp",EDGE,"E11.0");var subQ2=makeQuery(id+"F2.imprint","INTERSECT",VERTEX,{"derivedFrom":[subQ1,subQ0]});Q55=makeQuery(id+"F2.imprint","IMPRINT",FACE,{"disambiguationData":[TD([[makeQuery(id+"F2.imprint","IMPRINT",EDGE,{"disambiguationData":[TD([[subQ2,-1.0]])],"derivedFrom":subQ1}),-1.0]])]});}
            var Q56;
            {var subQ0=sQuery(id+"F2.wireOp",EDGE,"E19.0");var subQ1=sQuery(id+"F2.wireOp",EDGE,"E10.0");var subQ2=makeQuery(id+"F2.imprint","INTERSECT",VERTEX,{"derivedFrom":[subQ1,subQ0]});Q56=makeQuery(id+"F2.imprint","IMPRINT",FACE,{"disambiguationData":[TD([[makeQuery(id+"F2.imprint","IMPRINT",EDGE,{"disambiguationData":[TD([[subQ2,-1.0]])],"derivedFrom":subQ1}),-1.0]])]});}
            var Q57;
            {var subQ0=sQuery(id+"F2.wireOp",EDGE,"E17.0");var subQ1=sQuery(id+"F2.wireOp",EDGE,"E9.0");var subQ2=makeQuery(id+"F2.imprint","INTERSECT",VERTEX,{"derivedFrom":[subQ1,subQ0]});Q57=makeQuery(id+"F2.imprint","IMPRINT",FACE,{"disambiguationData":[TD([[makeQuery(id+"F2.imprint","IMPRINT",EDGE,{"disambiguationData":[TD([[subQ2,-1.0]])],"derivedFrom":subQ1}),-1.0]])]});}
            var Q58;
            {var subQ0=sQuery(id+"F2.wireOp",EDGE,"E20.0");var subQ1=sQuery(id+"F2.wireOp",EDGE,"E10.0");var subQ2=makeQuery(id+"F2.imprint","INTERSECT",VERTEX,{"derivedFrom":[subQ1,subQ0]});Q58=makeQuery(id+"F2.imprint","IMPRINT",FACE,{"disambiguationData":[TD([[makeQuery(id+"F2.imprint","IMPRINT",EDGE,{"disambiguationData":[TD([[subQ2,-1.0]])],"derivedFrom":subQ1}),-1.0]])]});}
            var Q59;
            {var subQ0=sQuery(id+"F2.wireOp",EDGE,"E17.0");var subQ1=sQuery(id+"F2.wireOp",EDGE,"E8.0");var subQ2=makeQuery(id+"F2.imprint","INTERSECT",VERTEX,{"derivedFrom":[subQ1,subQ0]});Q59=makeQuery(id+"F2.imprint","IMPRINT",FACE,{"disambiguationData":[TD([[makeQuery(id+"F2.imprint","IMPRINT",EDGE,{"disambiguationData":[TD([[subQ2,-1.0]])],"derivedFrom":subQ1}),-1.0]])]});}
            var Q60;
            {var subQ0=sQuery(id+"F2.wireOp",EDGE,"E17.0");var subQ1=sQuery(id+"F2.wireOp",EDGE,"E10.0");var subQ2=makeQuery(id+"F2.imprint","INTERSECT",VERTEX,{"derivedFrom":[subQ1,subQ0]});Q60=makeQuery(id+"F2.imprint","IMPRINT",FACE,{"disambiguationData":[TD([[makeQuery(id+"F2.imprint","IMPRINT",EDGE,{"disambiguationData":[TD([[subQ2,-1.0]])],"derivedFrom":subQ1}),-1.0]])]});}
            var Q61;
            {var subQ0=sQuery(id+"F2.wireOp",EDGE,"E15.0");var subQ1=sQuery(id+"F2.wireOp",EDGE,"E8.0");var subQ2=makeQuery(id+"F2.imprint","INTERSECT",VERTEX,{"derivedFrom":[subQ1,subQ0]});Q61=makeQuery(id+"F2.imprint","IMPRINT",FACE,{"disambiguationData":[TD([[makeQuery(id+"F2.imprint","IMPRINT",EDGE,{"disambiguationData":[TD([[subQ2,-1.0]])],"derivedFrom":subQ1}),-1.0]])]});}
            var Q62;
            {var subQ0=sQuery(id+"F2.wireOp",EDGE,"E15.0");var subQ1=sQuery(id+"F2.wireOp",EDGE,"E10.0");var subQ2=makeQuery(id+"F2.imprint","INTERSECT",VERTEX,{"derivedFrom":[subQ1,subQ0]});Q62=makeQuery(id+"F2.imprint","IMPRINT",FACE,{"disambiguationData":[TD([[makeQuery(id+"F2.imprint","IMPRINT",EDGE,{"disambiguationData":[TD([[subQ2,-1.0]])],"derivedFrom":subQ1}),-1.0]])]});}
            extrude(context, id + "F3", {"entities" : qUnion([Q0, Q1, Q2, Q3, Q4, Q5, Q6, Q7, Q8, Q9, Q10, Q11, Q12, Q13, Q14, Q15, Q16, Q17, Q18, Q19, Q20, Q21, Q22, Q23, Q24, Q25, Q26, Q27, Q28, Q29, Q30, Q31, Q32, Q33, Q34, Q35, Q36, Q37, Q38, Q39, Q40, Q41, Q42, Q43, Q44, Q45, Q46, Q47, Q48, Q49, Q50, Q51, Q52, Q53, Q54, Q55, Q56, Q57, Q58, Q59, Q60, Q61, Q62]), "operationType" : NewBodyOperationType.REMOVE, "oppositeDirection" : true, "depth" : 2 * mm});
        }
        {
            var Q0;
            {var subQ0=sQuery(id+"F2.wireOp",EDGE,"E16.0");var subQ1=sQuery(id+"F2.wireOp",EDGE,"E9.0");var subQ2=makeQuery(id+"F2.imprint","INTERSECT",VERTEX,{"derivedFrom":[subQ1,subQ0]});Q0=makeQuery(id+"F3.boolean.opBoolean","SPLIT",FACE,{"disambiguationData":[TD([makeQuery(id+"F3.opExtrude","SWEPT_FACE",FACE,{"disambiguationData":[OSD([subQ1]),TDD([makeQuery(id+"F2.imprint","IMPRINT",EDGE,{"disambiguationData":[TD([[subQ2,-1.0]])],"derivedFrom":subQ1})])]})])],"derivedFrom":makeQuery(id+"F1.opExtrude","CAP_FACE",FACE,{"disambiguationData":[OSD([sQuery(id+"F0.wireOp",EDGE,"E3"),sQuery(id+"F0.wireOp",EDGE,"E4"),sQuery(id+"F0.wireOp",EDGE,"E5")])],"isStart":false})});}
            var sketch = newSketch(context, id + "F4", { "sketchPlane" : qUnion([Q0])});
            skLineSegment(sketch, "E34.0", {"start": v(-40, -213.16) * mm, "end": v(-40, -295.55) * mm});
            skArc(sketch, "E35", {"start": v(0, -173.16) * mm, "mid": v(-28.28, -184.87) * mm, "end": v(-40, -213.16) * mm});
            skLineSegment(sketch, "E36", {"start": v(0, -173.16) * mm, "end": v(0, -300.1) * mm});
            skLineSegment(sketch, "E37", {"start": v(0, -300.1) * mm, "end": v(-40, -295.55) * mm});
            skSolve(sketch);
        }
        {
            var Q0;
            Q0 = qSketchRegion(id + "F4", true);
            extrude(context, id + "F5", {"entities" : qUnion([Q0]), "operationType" : NewBodyOperationType.REMOVE, "oppositeDirection" : true, "depth" : 10 * mm});
        }
        {
            var Q0;
            {var subQ0=sQuery(id+"F2.wireOp",EDGE,"E18.0");var subQ1=sQuery(id+"F2.wireOp",EDGE,"E9.0");var subQ2=makeQuery(id+"F2.imprint","INTERSECT",VERTEX,{"derivedFrom":[subQ1,subQ0]});Q0=makeQuery(id+"F3.boolean.opBoolean","SPLIT",FACE,{"disambiguationData":[TD([makeQuery(id+"F3.opExtrude","SWEPT_FACE",FACE,{"disambiguationData":[OSD([subQ1]),TDD([makeQuery(id+"F2.imprint","IMPRINT",EDGE,{"disambiguationData":[TD([[subQ2,-1.0]])],"derivedFrom":subQ1})])]})])],"derivedFrom":makeQuery(id+"F1.opExtrude","CAP_FACE",FACE,{"disambiguationData":[OSD([sQuery(id+"F0.wireOp",EDGE,"E3"),sQuery(id+"F0.wireOp",EDGE,"E4"),sQuery(id+"F0.wireOp",EDGE,"E5")])],"isStart":false})});}
            var sketch = newSketch(context, id + "F6", { "sketchPlane" : qUnion([Q0])});
            skArc(sketch, "E38.0", {"start": v(-52, -298.98) * mm, "mid": v(-20.4, -306.26) * mm, "end": v(12, -307.1) * mm});
            skLineSegment(sketch, "E38.1", {"start": v(-52, -213.16) * mm, "end": v(-52, -298.98) * mm});
            skArc(sketch, "E38.2", {"start": v(12, -162.56) * mm, "mid": v(-32.25, -172.37) * mm, "end": v(-52, -213.16) * mm});
            skLineSegment(sketch, "E38.3", {"start": v(12, -307.1) * mm, "end": v(12, -162.56) * mm});
            skLineSegment(sketch, "E39", {"start": v(-8.3, -179.59) * mm, "end": v(-11.27, -156.27) * mm});
            skLineSegment(sketch, "E40", {"start": v(-11.27, -156.27) * mm, "end": v(7.43, -156.27) * mm});
            skLineSegment(sketch, "E41", {"start": v(7.43, -156.27) * mm, "end": v(7.43, -180.13) * mm});
            skLineSegment(sketch, "E42", {"start": v(7.43, -180.13) * mm, "end": v(-8.3, -179.59) * mm});
            skLineSegment(sketch, "E43", {"start": v(-27.66, -189.17) * mm, "end": v(-40.44, -175.93) * mm});
            skLineSegment(sketch, "E44", {"start": v(-40.44, -175.93) * mm, "end": v(-50.65, -188.6) * mm});
            skLineSegment(sketch, "E45", {"start": v(-50.65, -188.6) * mm, "end": v(-32.82, -198.02) * mm});
            skLineSegment(sketch, "E46", {"start": v(-32.82, -198.02) * mm, "end": v(-27.66, -189.17) * mm});
            skLineSegment(sketch, "E47", {"start": v(-37.34, -229.97) * mm, "end": v(-56.49, -229.97) * mm});
            skLineSegment(sketch, "E48", {"start": v(-56.49, -229.97) * mm, "end": v(-56.49, -217.85) * mm});
            skLineSegment(sketch, "E49", {"start": v(-56.49, -217.85) * mm, "end": v(-37.62, -217.85) * mm});
            skLineSegment(sketch, "E50", {"start": v(-37.62, -217.85) * mm, "end": v(-37.34, -229.97) * mm});
            skLineSegment(sketch, "E51", {"start": v(-49.6, -260.97) * mm, "end": v(-65.98, -292.53) * mm});
            skLineSegment(sketch, "E52", {"start": v(-65.98, -292.53) * mm, "end": v(-46.49, -298.05) * mm});
            skLineSegment(sketch, "E53", {"start": v(-46.49, -298.05) * mm, "end": v(-30.14, -265.12) * mm});
            skLineSegment(sketch, "E54", {"start": v(-30.14, -265.12) * mm, "end": v(-49.6, -260.97) * mm});
            skArc(sketch, "E55.0", {"start": v(12, -175) * mm, "mid": v(-23.66, -180.9) * mm, "end": v(-40, -213.16) * mm});
            skLineSegment(sketch, "E55.1", {"start": v(0, -295.55) * mm, "end": v(0, -173.16) * mm});
            skArc(sketch, "E55.2", {"start": v(-40, -290.12) * mm, "mid": v(-20.18, -294.19) * mm, "end": v(0, -295.55) * mm});
            skLineSegment(sketch, "E55.3", {"start": v(-40, -213.16) * mm, "end": v(-40, -302.53) * mm});
            skSolve(sketch);
        }
        {
            var Q0;
            {var subQ0=sQuery(id+"F6.wireOp",EDGE,"E49");var subQ1=sQuery(id+"F6.wireOp",EDGE,"E38.1");var subQ2=makeQuery(id+"F6.imprint","INTERSECT",VERTEX,{"derivedFrom":[subQ1,subQ0]});Q0=makeQuery(id+"F6.imprint","IMPRINT",FACE,{"disambiguationData":[TD([[makeQuery(id+"F6.imprint","IMPRINT",EDGE,{"disambiguationData":[TD([[subQ2,-1.0]])],"derivedFrom":subQ1}),1.0]])]});}
            var Q1;
            {var subQ0=sQuery(id+"F6.wireOp",EDGE,"E45");var subQ1=sQuery(id+"F6.wireOp",EDGE,"E38.2");var subQ2=makeQuery(id+"F6.imprint","INTERSECT",VERTEX,{"derivedFrom":[subQ1,subQ0]});Q1=makeQuery(id+"F6.imprint","IMPRINT",FACE,{"disambiguationData":[TD([[makeQuery(id+"F6.imprint","IMPRINT",EDGE,{"disambiguationData":[TD([[subQ2,-1.0]])],"derivedFrom":subQ0}),-1.0]])]});}
            var Q2;
            {var subQ0=sQuery(id+"F6.wireOp",EDGE,"E43");var subQ1=sQuery(id+"F6.wireOp",EDGE,"E38.2");var subQ2=makeQuery(id+"F6.imprint","INTERSECT",VERTEX,{"derivedFrom":[subQ1,subQ0]});Q2=makeQuery(id+"F6.imprint","IMPRINT",FACE,{"disambiguationData":[TD([[makeQuery(id+"F6.imprint","IMPRINT",EDGE,{"disambiguationData":[TD([[subQ2,-1.0]])],"derivedFrom":subQ1}),1.0]])]});}
            var Q3;
            {var subQ0=sQuery(id+"F6.wireOp",EDGE,"E39");var subQ1=sQuery(id+"F6.wireOp",EDGE,"E38.2");var subQ2=makeQuery(id+"F6.imprint","INTERSECT",VERTEX,{"derivedFrom":[subQ1,subQ0]});Q3=makeQuery(id+"F6.imprint","IMPRINT",FACE,{"disambiguationData":[TD([[makeQuery(id+"F6.imprint","IMPRINT",EDGE,{"disambiguationData":[TD([[subQ2,-1.0]])],"derivedFrom":subQ1}),1.0]])]});}
            var Q4;
            {var subQ2=sQuery(id+"F6.wireOp",EDGE,"E41");var subQ4=sQuery(id+"F6.wireOp",EDGE,"E38.2");var subQ5=makeQuery(id+"F6.imprint","INTERSECT",VERTEX,{"derivedFrom":[subQ4,subQ2]});Q4=makeQuery(id+"F6.imprint","IMPRINT",FACE,{"disambiguationData":[TD([[makeQuery(id+"F6.imprint","IMPRINT",EDGE,{"disambiguationData":[TD([[subQ5,-1.0]])],"derivedFrom":subQ4}),1.0]])]});}
            var Q5;
            {var subQ7=sQuery(id+"F6.wireOp",EDGE,"E38.1");var subQ10=sQuery(id+"F6.wireOp",EDGE,"E38.2");var subQ11=makeQuery(id+"F6.imprint","INTERSECT",VERTEX,{"derivedFrom":[subQ7,subQ10]});Q5=makeQuery(id+"F6.imprint","IMPRINT",FACE,{"disambiguationData":[TD([[makeQuery(id+"F6.imprint","IMPRINT",EDGE,{"disambiguationData":[TD([[subQ11,-1.0]])],"derivedFrom":subQ7}),1.0]])]});}
            var Q6;
            {var subQ0=sQuery(id+"F6.wireOp",EDGE,"E47");var subQ1=sQuery(id+"F6.wireOp",EDGE,"E38.1");var subQ2=makeQuery(id+"F6.imprint","INTERSECT",VERTEX,{"derivedFrom":[subQ1,subQ0]});Q6=makeQuery(id+"F6.imprint","IMPRINT",FACE,{"disambiguationData":[TD([[makeQuery(id+"F6.imprint","IMPRINT",EDGE,{"disambiguationData":[TD([[subQ2,1.0]])],"derivedFrom":subQ0}),1.0]])]});}
            var Q7;
            {var subQ4=sQuery(id+"F6.wireOp",EDGE,"E54");var subQ6=sQuery(id+"F6.wireOp",EDGE,"E51");var subQ7=makeQuery(id+"F6.imprint","INTERSECT",VERTEX,{"derivedFrom":[subQ6,subQ4]});Q7=makeQuery(id+"F6.imprint","IMPRINT",FACE,{"disambiguationData":[TD([[makeQuery(id+"F6.imprint","IMPRINT",EDGE,{"disambiguationData":[TD([[subQ7,-1.0]])],"derivedFrom":subQ6}),-1.0]])]});}
            var Q8;
            {var subQ3=sQuery(id+"F6.wireOp",EDGE,"E38.1");var subQ8=sQuery(id+"F6.wireOp",EDGE,"E51");var subQ10=makeQuery(id+"F6.imprint","INTERSECT",VERTEX,{"derivedFrom":[subQ3,subQ8]});Q8=makeQuery(id+"F6.imprint","IMPRINT",FACE,{"disambiguationData":[TD([[makeQuery(id+"F6.imprint","IMPRINT",EDGE,{"disambiguationData":[TD([[subQ10,-1.0]])],"derivedFrom":subQ3}),1.0]])]});}
            var Q9;
            {var subQ6=sQuery(id+"F6.wireOp",EDGE,"E38.0");var subQ8=sQuery(id+"F6.wireOp",EDGE,"E38.1");var subQ10=makeQuery(id+"F6.imprint","INTERSECT",VERTEX,{"derivedFrom":[subQ6,subQ8]});Q9=makeQuery(id+"F6.imprint","IMPRINT",FACE,{"disambiguationData":[TD([[makeQuery(id+"F6.imprint","IMPRINT",EDGE,{"disambiguationData":[TD([[subQ10,-1.0]])],"derivedFrom":subQ6}),1.0]])]});}
            extrude(context, id + "F7", {"entities" : qUnion([Q0, Q1, Q2, Q3, Q4, Q5, Q6, Q7, Q8, Q9]), "operationType" : NewBodyOperationType.ADD, "depth" : 5 * mm});
        }
        {
            var Q0;
            {var subQ0=sQuery(id+"F2.wireOp",EDGE,"E18.0");var subQ1=sQuery(id+"F2.wireOp",EDGE,"E9.0");var subQ2=makeQuery(id+"F2.imprint","INTERSECT",VERTEX,{"derivedFrom":[subQ1,subQ0]});Q0=makeQuery(id+"F3.boolean.opBoolean","SPLIT",FACE,{"disambiguationData":[TD([makeQuery(id+"F3.opExtrude","SWEPT_FACE",FACE,{"disambiguationData":[OSD([subQ1]),TDD([makeQuery(id+"F2.imprint","IMPRINT",EDGE,{"disambiguationData":[TD([[subQ2,-1.0]])],"derivedFrom":subQ1})])]})])],"derivedFrom":makeQuery(id+"F1.opExtrude","CAP_FACE",FACE,{"disambiguationData":[OSD([sQuery(id+"F0.wireOp",EDGE,"E3"),sQuery(id+"F0.wireOp",EDGE,"E4"),sQuery(id+"F0.wireOp",EDGE,"E5")])],"isStart":false})});}
            var sketch = newSketch(context, id + "F8", { "sketchPlane" : qUnion([Q0])});
            skLineSegment(sketch, "E56", {"start": v(2.96, -155.61) * mm, "end": v(-9.95, -155.61) * mm});
            skLineSegment(sketch, "E57", {"start": v(-9.95, -155.61) * mm, "end": v(-5.94, -178.7) * mm});
            skLineSegment(sketch, "E58", {"start": v(-5.94, -178.7) * mm, "end": v(3.82, -178.7) * mm});
            skLineSegment(sketch, "E59", {"start": v(3.82, -178.7) * mm, "end": v(2.96, -155.61) * mm});
            skLineSegment(sketch, "E60", {"start": v(-27.05, -190.07) * mm, "end": v(-38.18, -171.64) * mm});
            skLineSegment(sketch, "E61", {"start": v(-38.18, -171.64) * mm, "end": v(-51.04, -185.38) * mm});
            skLineSegment(sketch, "E62", {"start": v(-51.04, -185.38) * mm, "end": v(-31.05, -197.72) * mm});
            skLineSegment(sketch, "E63", {"start": v(-31.05, -197.72) * mm, "end": v(-27.05, -190.07) * mm});
            skLineSegment(sketch, "E64.bottom", {"start": v(-32.87, -215.82) * mm, "end": v(-58.04, -215.82) * mm});
            skLineSegment(sketch, "E64.top", {"start": v(-32.87, -232.02) * mm, "end": v(-58.04, -232.02) * mm});
            skLineSegment(sketch, "E64.left", {"start": v(-32.87, -215.82) * mm, "end": v(-32.87, -232.02) * mm});
            skLineSegment(sketch, "E64.right", {"start": v(-58.04, -215.82) * mm, "end": v(-58.04, -232.02) * mm});
            skLineSegment(sketch, "E65", {"start": v(-35.37, -266.33) * mm, "end": v(-53.53, -266.33) * mm});
            skLineSegment(sketch, "E66", {"start": v(-53.53, -266.33) * mm, "end": v(-59.2, -290) * mm});
            skLineSegment(sketch, "E67", {"start": v(-59.2, -290) * mm, "end": v(-37.54, -293.82) * mm});
            skLineSegment(sketch, "E68", {"start": v(-37.54, -293.82) * mm, "end": v(-35.37, -266.33) * mm});
            skSolve(sketch);
        }
        {
            var Q0;
            Q0 = qSketchRegion(id + "F8", true);
            extrude(context, id + "F9", {"entities" : qUnion([Q0]), "operationType" : NewBodyOperationType.ADD, "depth" : 8 * mm});
        }
        {
            var Q0;
            {var subQ0=sQuery(id+"F2.wireOp",EDGE,"E18.0");var subQ1=sQuery(id+"F2.wireOp",EDGE,"E7.0");var subQ2=makeQuery(id+"F2.imprint","INTERSECT",VERTEX,{"derivedFrom":[subQ1,subQ0]});Q0=makeQuery(id+"F3.boolean.opBoolean","SPLIT",FACE,{"disambiguationData":[TD([makeQuery(id+"F3.opExtrude","SWEPT_FACE",FACE,{"disambiguationData":[OSD([subQ1]),TDD([makeQuery(id+"F2.imprint","IMPRINT",EDGE,{"disambiguationData":[TD([[subQ2,-1.0]])],"derivedFrom":subQ1})])]})])],"derivedFrom":makeQuery(id+"F1.opExtrude","CAP_FACE",FACE,{"disambiguationData":[OSD([sQuery(id+"F0.wireOp",EDGE,"E3"),sQuery(id+"F0.wireOp",EDGE,"E4"),sQuery(id+"F0.wireOp",EDGE,"E5")])],"isStart":false})});}
            var sketch = newSketch(context, id + "F10", { "sketchPlane" : qUnion([Q0])});
            skLineSegment(sketch, "E69", {"start": v(0, -139.94) * mm, "end": v(0, -313.71) * mm});
            skLineSegment(sketch, "E70", {"start": v(0, -139.94) * mm, "end": v(23.55, -139.94) * mm});
            skLineSegment(sketch, "E71", {"start": v(23.55, -139.94) * mm, "end": v(19.63, -313.71) * mm});
            skLineSegment(sketch, "E72", {"start": v(19.63, -313.71) * mm, "end": v(0, -313.71) * mm});
            skCircle(sketch, "E73", {"center": v(0, -145.51) * mm, "radius": 150 * mm});
            skCircle(sketch, "E74.0", {"center": v(0, -145.51) * mm, "radius": 180 * mm});
            skSolve(sketch);
        }
        {
            var Q0;
            {var subQ0=sQuery(id+"F10.wireOp",EDGE,"E70");Q0=makeQuery(id+"F10.imprint","IMPRINT",FACE,{"disambiguationData":[TD([[makeQuery(id+"F10.imprint","IMPRINT",EDGE,{"derivedFrom":subQ0}),-1.0]])]});}
            var Q1;
            {var subQ0=sQuery(id+"F10.wireOp",EDGE,"E72");Q1=makeQuery(id+"F10.imprint","IMPRINT",FACE,{"disambiguationData":[TD([[makeQuery(id+"F10.imprint","IMPRINT",EDGE,{"derivedFrom":subQ0}),-1.0]])]});}
            var Q2;
            {var subQ0=sQuery(id+"F10.wireOp",EDGE,"E72");Q2=makeQuery(id+"F10.imprint","IMPRINT",FACE,{"disambiguationData":[TD([[makeQuery(id+"F10.imprint","IMPRINT",EDGE,{"derivedFrom":subQ0}),1.0]])]});}
            extrude(context, id + "F11", {"entities" : qUnion([Q0, Q1, Q2]), "operationType" : NewBodyOperationType.REMOVE, "depth" : 114 * mm});
        }
        {
            var Q0;
            Q0=makeQuery(id+"F5.boolean.opBoolean","COPY",FACE,{"derivedFrom":makeQuery(id+"F5.opExtrude","CAP_FACE",FACE,{"disambiguationData":[OSD([sQuery(id+"F4.wireOp",EDGE,"E34.0"),sQuery(id+"F4.wireOp",EDGE,"E35"),sQuery(id+"F4.wireOp",EDGE,"E36"),sQuery(id+"F4.wireOp",EDGE,"E37")])],"isStart":false})});
            extrude(context, id + "F12", {"entities" : qUnion([Q0]), "operationType" : NewBodyOperationType.REMOVE, "depth" : 25 * mm});
        }
        {
            var Q0;
            Q0=makeQuery(id+"F1.opExtrude","SWEPT_BODY",BODY,{"disambiguationData":[OSD([sQuery(id+"F0.wireOp",EDGE,"E3"),sQuery(id+"F0.wireOp",EDGE,"E4"),sQuery(id+"F0.wireOp",EDGE,"E5")])]});
            var Q1;
            Q1=qCreatedBy(makeId("Right.planeOp"),FACE);
            mirror(context, id + "F13", {"operationType" : NewBodyOperationType.ADD, "entities" : qUnion([Q0]), "mirrorPlane" : qUnion([Q1])});
        }
        {
            var Q0;
            {var subQ0=makeQuery(id+"F5.boolean.opBoolean","COPY",FACE,{"derivedFrom":makeQuery(id+"F5.opExtrude","CAP_FACE",FACE,{"disambiguationData":[OSD([sQuery(id+"F4.wireOp",EDGE,"E34.0"),sQuery(id+"F4.wireOp",EDGE,"E35"),sQuery(id+"F4.wireOp",EDGE,"E36"),sQuery(id+"F4.wireOp",EDGE,"E37")])],"isStart":false})});Q0=makeQuery(id+"F13.boolean.opBoolean","MERGE",FACE,{"derivedFrom":[subQ0,makeQuery(id+"F13.opPattern","COPY",FACE,{"derivedFrom":subQ0,"instanceName":"1"})]});}
            extrude(context, id + "F14", {"entities" : qUnion([Q0]), "operationType" : NewBodyOperationType.ADD, "depth" : 10.1 * mm});
        }
        {
            var Q0;
            Q0=qCreatedBy(makeId("Top.planeOp"),FACE);
            var sketch = newSketch(context, id + "F15", { "sketchPlane" : qUnion([Q0])});
            skLineSegment(sketch, "E75", {"start": v(0, 135.3) * mm, "end": v(0, -318.8) * mm, "construction": true});
            skLineSegment(sketch, "E76.0", {"start": v(-150, 44) * mm, "end": v(-150, -145.55) * mm});
            skLineSegment(sketch, "E77", {"start": v(-150, 44) * mm, "end": v(0, 44) * mm});
            skArc(sketch, "E78", {"start": v(-150, -145.55) * mm, "mid": v(-106.07, -251.62) * mm, "end": v(0, -295.55) * mm});
            skLineSegment(sketch, "E79", {"start": v(-150, -145.55) * mm, "end": v(0, -145.55) * mm});
            skLineSegment(sketch, "E80", {"start": v(0, -145.55) * mm, "end": v(0, -295.55) * mm});
            skSolve(sketch);
        }
        {
            var Q0;
            Q0=qCreatedBy(makeId("Top.planeOp"),FACE);
            var sketch = newSketch(context, id + "F16", { "sketchPlane" : qUnion([Q0])});
            skLineSegment(sketch, "E81", {"start": v(0, -145.55) * mm, "end": v(0, 7.99) * mm});
            skLineSegment(sketch, "E82", {"start": v(-30.54, 7.99) * mm, "end": v(-38.54, 7.99) * mm});
            skLineSegment(sketch, "E83", {"start": v(-38.54, 7.99) * mm, "end": v(-38.54, -2.01) * mm});
            skLineSegment(sketch, "E84", {"start": v(-38.54, -2.01) * mm, "end": v(-35, -5.55) * mm});
            skLineSegment(sketch, "E85", {"start": v(-35, -5.55) * mm, "end": v(-35, -18.55) * mm});
            skLineSegment(sketch, "E86", {"start": v(-35, -145.55) * mm, "end": v(0, -145.55) * mm});
            skArc(sketch, "E87", {"start": v(-35, -73.55) * mm, "mid": v(-37, -75.55) * mm, "end": v(-35, -77.55) * mm});
            skLineSegment(sketch, "E88.trimOffspring", {"start": v(-35, -77.55) * mm, "end": v(-35, -88.55) * mm});
            skLineSegment(sketch, "E89.0", {"start": v(-34, -18.55) * mm, "end": v(-34, -20.55) * mm});
            skLineSegment(sketch, "E90.0", {"start": v(-35, -20.55) * mm, "end": v(-34, -20.55) * mm});
            skLineSegment(sketch, "E91.0", {"start": v(-35, -18.55) * mm, "end": v(-34, -18.55) * mm});
            skLineSegment(sketch, "E92.0", {"start": v(-35, -32.55) * mm, "end": v(-34, -32.55) * mm});
            skLineSegment(sketch, "E93.0", {"start": v(-35, -34.55) * mm, "end": v(-34, -34.55) * mm});
            skLineSegment(sketch, "E94.0", {"start": v(-35, -46.55) * mm, "end": v(-34, -46.55) * mm});
            skLineSegment(sketch, "E95.0", {"start": v(-35, -48.55) * mm, "end": v(-34, -48.55) * mm});
            skLineSegment(sketch, "E96.0", {"start": v(-35, -60.55) * mm, "end": v(-34, -60.55) * mm});
            skLineSegment(sketch, "E97.0", {"start": v(-35, -62.55) * mm, "end": v(-34, -62.55) * mm});
            skLineSegment(sketch, "E98.trimOffspring", {"start": v(-34, -32.55) * mm, "end": v(-34, -34.55) * mm});
            skLineSegment(sketch, "E99.trimOffspring", {"start": v(-34, -46.55) * mm, "end": v(-34, -48.55) * mm});
            skLineSegment(sketch, "E100.trimOffspring", {"start": v(-34, -60.55) * mm, "end": v(-34, -62.55) * mm});
            skLineSegment(sketch, "E101.trimOffspring", {"start": v(-35, -20.55) * mm, "end": v(-35, -32.55) * mm});
            skLineSegment(sketch, "E102.trimOffspring", {"start": v(-35, -34.55) * mm, "end": v(-35, -46.55) * mm});
            skLineSegment(sketch, "E103.trimOffspring", {"start": v(-35, -48.55) * mm, "end": v(-35, -60.55) * mm});
            skLineSegment(sketch, "E104.trimOffspring", {"start": v(-35, -62.55) * mm, "end": v(-35, -73.55) * mm});
            skLineSegment(sketch, "E105.MirrorCS", {"start": v(-35, -88.55) * mm, "end": v(-34, -88.55) * mm});
            skLineSegment(sketch, "E106.MirrorCS", {"start": v(-35, -104.55) * mm, "end": v(-34, -104.55) * mm});
            skLineSegment(sketch, "E107.MirrorCS", {"start": v(-35, -116.55) * mm, "end": v(-34, -116.55) * mm});
            skLineSegment(sketch, "E108.MirrorCS", {"start": v(-34, -118.55) * mm, "end": v(-34, -116.55) * mm});
            skLineSegment(sketch, "E109.MirrorCS", {"start": v(-35, -90.55) * mm, "end": v(-34, -90.55) * mm});
            skLineSegment(sketch, "E110.MirrorCS", {"start": v(-34, -104.55) * mm, "end": v(-34, -102.55) * mm});
            skLineSegment(sketch, "E111.MirrorCS", {"start": v(-35, -132.55) * mm, "end": v(-34, -132.55) * mm});
            skLineSegment(sketch, "E112.MirrorCS", {"start": v(-35, -102.55) * mm, "end": v(-34, -102.55) * mm});
            skLineSegment(sketch, "E113.MirrorCS", {"start": v(-35, -130.55) * mm, "end": v(-34, -130.55) * mm});
            skLineSegment(sketch, "E114.MirrorCS", {"start": v(-34, -90.55) * mm, "end": v(-34, -88.55) * mm});
            skLineSegment(sketch, "E115.MirrorCS", {"start": v(-35, -118.55) * mm, "end": v(-34, -118.55) * mm});
            skLineSegment(sketch, "E116.MirrorCS", {"start": v(-34, -132.55) * mm, "end": v(-34, -130.55) * mm});
            skLineSegment(sketch, "E117.MirrorCS", {"start": v(-35, -102.55) * mm, "end": v(-35, -90.55) * mm});
            skLineSegment(sketch, "E118.MirrorCS", {"start": v(-35, -116.55) * mm, "end": v(-35, -104.55) * mm});
            skLineSegment(sketch, "E119.MirrorCS", {"start": v(-35, -130.55) * mm, "end": v(-35, -118.55) * mm});
            skLineSegment(sketch, "E120.trimOffspring", {"start": v(-35, -90.55) * mm, "end": v(-35, -102.55) * mm});
            skLineSegment(sketch, "E121.trimOffspring", {"start": v(-35, -118.55) * mm, "end": v(-35, -130.55) * mm});
            skLineSegment(sketch, "E122.trimOffspring", {"start": v(-35, -132.55) * mm, "end": v(-35, -145.55) * mm});
            skLineSegment(sketch, "E123.0", {"start": v(-30.54, 7.99) * mm, "end": v(-30.54, 2.99) * mm});
            skLineSegment(sketch, "E124.0", {"start": v(0, 2.99) * mm, "end": v(-30.54, 2.99) * mm});
            skSolve(sketch);
        }
        {
            var Q0;
            Q0 = qSketchRegion(id + "F16", true);
            var Q1;
            Q1=sQuery(id+"F16.wireOp",EDGE,"E81");
            revolve(context, id + "F17", {"operationType" : NewBodyOperationType.ADD, "entities" : qUnion([Q0]), "axis" : qUnion([Q1]), "revolveType" : RevolveType.ONE_DIRECTION, "angle" : 90 * degree});
        }
        {
            var Q0;
            Q0=qCreatedBy(makeId("Top.planeOp"),FACE);
            var sketch = newSketch(context, id + "F18", { "sketchPlane" : qUnion([Q0])});
            skLineSegment(sketch, "E125.0", {"start": v(-84.05, -145.55) * mm, "end": v(0, -145.55) * mm});
            skLineSegment(sketch, "E126", {"start": v(-70.55, -145.55) * mm, "end": v(-70.55, -85.02) * mm});
            skPoint(sketch, "E127.orphan", {"position": v(-150, -145.55) * mm});
            skLineSegment(sketch, "E128.0", {"start": v(-85.55, -145.55) * mm, "end": v(-85.55, -132.55) * mm});
            skLineSegment(sketch, "E129", {"start": v(-85.55, -91.58) * mm, "end": v(-92.12, -85.02) * mm});
            skLineSegment(sketch, "E130", {"start": v(-92.12, -85.02) * mm, "end": v(-92.12, -78.02) * mm});
            skLineSegment(sketch, "E131", {"start": v(-70.55, -85.02) * mm, "end": v(-70.55, -81.52) * mm});
            skLineSegment(sketch, "E132", {"start": v(-92.12, -78.02) * mm, "end": v(-87.55, -78.02) * mm});
            skLineSegment(sketch, "E133", {"start": v(-87.55, -78.02) * mm, "end": v(-87.55, -81.52) * mm});
            skLineSegment(sketch, "E134", {"start": v(-87.55, -81.52) * mm, "end": v(-70.55, -81.52) * mm});
            skPoint(sketch, "E135.orphan", {"position": v(-70.55, -78.02) * mm});
            skLineSegment(sketch, "E136.0", {"start": v(-84.55, -132.55) * mm, "end": v(-84.55, -130.55) * mm});
            skLineSegment(sketch, "E137.trimOffspring", {"start": v(-84.55, -104.55) * mm, "end": v(-84.55, -102.55) * mm});
            skLineSegment(sketch, "E138.trimOffspring", {"start": v(-84.55, -102.55) * mm, "end": v(-85.55, -102.55) * mm});
            skLineSegment(sketch, "E139.trimOffspring", {"start": v(-84.55, -104.55) * mm, "end": v(-85.55, -104.55) * mm});
            skLineSegment(sketch, "E140.trimOffspring", {"start": v(-84.55, -116.55) * mm, "end": v(-85.55, -116.55) * mm});
            skLineSegment(sketch, "E141.trimOffspring", {"start": v(-84.55, -118.55) * mm, "end": v(-85.55, -118.55) * mm});
            skLineSegment(sketch, "E142.trimOffspring", {"start": v(-84.55, -118.55) * mm, "end": v(-84.55, -116.55) * mm});
            skLineSegment(sketch, "E143.trimOffspring", {"start": v(-84.55, -132.55) * mm, "end": v(-85.55, -132.55) * mm});
            skLineSegment(sketch, "E144.trimOffspring", {"start": v(-84.55, -130.55) * mm, "end": v(-85.55, -130.55) * mm});
            skLineSegment(sketch, "E145.trimOffspring", {"start": v(-85.55, -102.55) * mm, "end": v(-85.55, -91.58) * mm});
            skLineSegment(sketch, "E146.trimOffspring", {"start": v(-85.55, -116.55) * mm, "end": v(-85.55, -104.55) * mm});
            skLineSegment(sketch, "E147.trimOffspring", {"start": v(-85.55, -130.55) * mm, "end": v(-85.55, -118.55) * mm});
            skLineSegment(sketch, "E148", {"start": v(-85.55, -145.55) * mm, "end": v(-70.55, -145.55) * mm});
            skSolve(sketch);
        }
        {
            var Q0;
            Q0 = qSketchRegion(id + "F18", true);
            var Q1;
            Q1=sQuery(id+"F18.wireOp",EDGE,"E126");
            revolve(context, id + "F19", {"operationType" : NewBodyOperationType.ADD, "entities" : qUnion([Q0]), "axis" : qUnion([Q1]), "revolveType" : RevolveType.TWO_DIRECTIONS, "angle" : 180 * degree, "angleBack" : 0 * degree});
        }
    });
